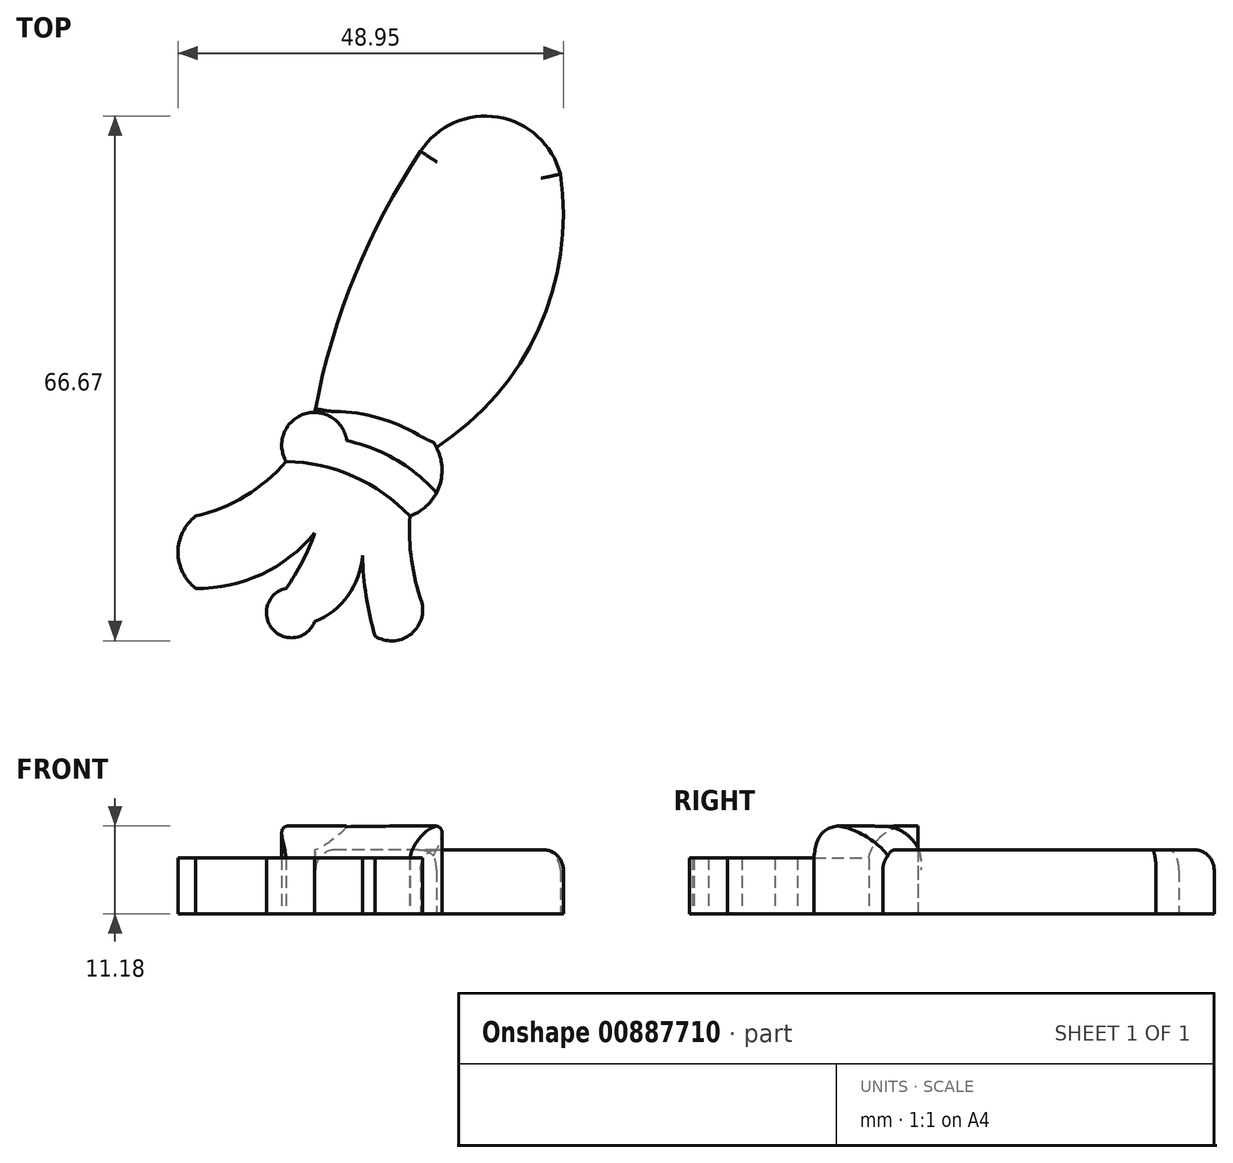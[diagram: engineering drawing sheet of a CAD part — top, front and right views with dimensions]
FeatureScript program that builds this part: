
annotation { "Feature Type Name" : "Feature", "Feature Type Description" : "" }
export const myFeature = defineFeature(function(context is Context, id is Id, definition is map)
    precondition{}
    {
        {
            var Q0;
            Q0=qCreatedBy(makeId("Top.planeOp"),FACE);
            var sketch = newSketch(context, id + "F0", { "sketchPlane" : qUnion([Q0])});
            skArc(sketch, "E0", {"start": v(-8.39, 28.06) * mm, "mid": v(-16.78, 12.16) * mm, "end": v(-21.82, -5.1) * mm});
            skArc(sketch, "E1", {"start": v(-6.36, -9.54) * mm, "mid": v(6.62, 5.48) * mm, "end": v(9.38, 25.15) * mm});
            skArc(sketch, "E2", {"start": v(-6.36, -9.54) * mm, "mid": v(-13.66, -5.82) * mm, "end": v(-21.82, -5.1) * mm});
            skArc(sketch, "E3", {"start": v(-9.74, -18.3) * mm, "mid": v(-6.07, -14.69) * mm, "end": v(-6.36, -9.54) * mm});
            skArc(sketch, "E4", {"start": v(-9.74, -18.3) * mm, "mid": v(-16.9, -13.23) * mm, "end": v(-25.46, -11.34) * mm});
            skArc(sketch, "E5", {"start": v(-21.82, -5.1) * mm, "mid": v(-25.45, -7.17) * mm, "end": v(-25.46, -11.34) * mm});
            skArc(sketch, "E6", {"start": v(-36.94, -18.3) * mm, "mid": v(-30.64, -15.74) * mm, "end": v(-25.46, -11.34) * mm});
            skArc(sketch, "E7", {"start": v(-36.94, -18.3) * mm, "mid": v(-39.2, -22.88) * mm, "end": v(-36.94, -27.46) * mm});
            skArc(sketch, "E8", {"start": v(-36.94, -27.46) * mm, "mid": v(-28.58, -25.67) * mm, "end": v(-21.82, -20.42) * mm});
            skArc(sketch, "E9", {"start": v(-25.46, -27.46) * mm, "mid": v(-23.39, -24.07) * mm, "end": v(-21.82, -20.42) * mm});
            skArc(sketch, "E10", {"start": v(-25.46, -27.46) * mm, "mid": v(-27.2, -32.63) * mm, "end": v(-21.82, -31.7) * mm});
            skArc(sketch, "E11", {"start": v(-21.82, -31.7) * mm, "mid": v(-17.57, -28.36) * mm, "end": v(-15.75, -23.27) * mm});
            skArc(sketch, "E12", {"start": v(-15.75, -23.27) * mm, "mid": v(-15.3, -28.46) * mm, "end": v(-14.16, -33.54) * mm});
            skArc(sketch, "E13", {"start": v(-14.16, -33.54) * mm, "mid": v(-9.78, -33.4) * mm, "end": v(-8.19, -29.32) * mm});
            skArc(sketch, "E14", {"start": v(-9.74, -18.3) * mm, "mid": v(-9.53, -23.89) * mm, "end": v(-8.19, -29.32) * mm});
            skArc(sketch, "E15", {"start": v(9.38, 25.15) * mm, "mid": v(1.45, 32.4) * mm, "end": v(-8.39, 28.06) * mm});
            skSolve(sketch);
        }
        {
            var Q0;
            Q0=makeQuery(id+"F0.imprint","IMPRINT",FACE,{"disambiguationData":[TD([[makeQuery(id+"F0.imprint","IMPRINT",EDGE,{"derivedFrom":sQuery(id+"F0.wireOp",EDGE,"E0")}),1.0]])]});
            extrude(context, id + "F1", {"entities" : qUnion([Q0]), "depth" : 8.13 * mm, "offsetDistance" : 25.4 * mm});
        }
        {
            var Q0;
            Q0=makeQuery(id+"F0.imprint","IMPRINT",FACE,{"disambiguationData":[TD([[makeQuery(id+"F0.imprint","IMPRINT",EDGE,{"derivedFrom":sQuery(id+"F0.wireOp",EDGE,"E2")}),1.0]])]});
            extrude(context, id + "F2", {"entities" : qUnion([Q0]), "operationType" : NewBodyOperationType.ADD, "depth" : 11.18 * mm, "offsetDistance" : 25.4 * mm});
        }
        {
            var Q0;
            Q0=makeQuery(id+"F0.imprint","IMPRINT",FACE,{"disambiguationData":[TD([[makeQuery(id+"F0.imprint","IMPRINT",EDGE,{"derivedFrom":sQuery(id+"F0.wireOp",EDGE,"E4")}),1.0]])]});
            extrude(context, id + "F3", {"entities" : qUnion([Q0]), "operationType" : NewBodyOperationType.ADD, "depth" : 7.11 * mm, "offsetDistance" : 25.4 * mm});
        }
        {
            var Q0;
            Q0=makeQuery(id+"F2.opExtrude","CAP_EDGE",EDGE,{"disambiguationData":[OSD([sQuery(id+"F0.wireOp",EDGE,"E4")])],"isStart":false});
            var Q1;
            Q1=makeQuery(id+"F2.opExtrude","CAP_EDGE",EDGE,{"disambiguationData":[OSD([sQuery(id+"F0.wireOp",EDGE,"E2")])],"isStart":false});
            fillet(context, id + "F4", {"entities" : qUnion([Q0, Q1]), "radius" : 5.08 * mm, "tangentPropagation" : true, "allowEdgeOverflow" : false});
        }
        {
            var Q0;
            Q0=makeQuery(id+"F1.opExtrude","CAP_EDGE",EDGE,{"disambiguationData":[OSD([sQuery(id+"F0.wireOp",EDGE,"E1")])],"isStart":false});
            var Q1;
            Q1=makeQuery(id+"F1.opExtrude","CAP_EDGE",EDGE,{"disambiguationData":[OSD([sQuery(id+"F0.wireOp",EDGE,"E0")])],"isStart":false});
            var Q2;
            Q2=makeQuery(id+"F1.opExtrude","CAP_EDGE",EDGE,{"disambiguationData":[OSD([sQuery(id+"F0.wireOp",EDGE,"E15")])],"isStart":false});
            fillet(context, id + "F5", {"entities" : qUnion([Q0, Q1, Q2]), "radius" : 2.54 * mm, "tangentPropagation" : true, "allowEdgeOverflow" : false});
        }
    });
